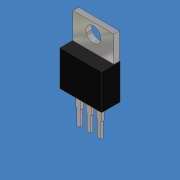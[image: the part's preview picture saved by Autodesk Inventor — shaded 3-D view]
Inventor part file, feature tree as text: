
AUTODESK INVENTOR PART (.ipt)
format: ipt  version: 2014 SP1 (Build 180222100, 222)  size: 157,184 bytes
history: native  units: mm (DEFAULTED — no unit token found)
features: sketch x5, extrude x4, hole x1, pattern_linear x1
ambient origin geometry x8: Origin, YZ Plane, XZ Plane, XY Plane, X Axis, Y Axis, Z Axis, Center Point
bodies: Solid1 (feature_tree)
feature tree (11):
  extrude  "Extrusion1"  Depth=8.636mm
  extrude  "Extrusion2"  Depth=6.35mm TaperAngle=0.0deg
  hole  "Hole1"  [1 undecoded]
  extrude  "Extrusion3"  Depth=0.5842mm
  extrude  "Extrusion4"  Depth=1.27mm
  pattern_linear  "Rectangular Pattern1"  Spacing1=1.905mm  [1 undecoded]
  sketch  "Sketch1"  dims[d0=10.16mm d1=8.636mm]
  sketch  "Sketch2"  dims[d2=4.4704mm d3=0.0mm d5=6.35mm d6=0.0mm]
  sketch  "Sketch3"  dims[d7=1.397mm d8=9.9822mm]
  sketch  "Sketch4"  dims[d9=2.54mm]
  sketch  "Sketch5"  dims[d10=3.683mm d11=12.7mm d12=9.525mm d13=6.35mm d14=14.3117mm d15=19.05mm d16=20.594885mm d17=0.5842mm d18=1.27mm d19=1.905mm d20=3.81mm d21=0.0mm d22=0.8128mm d23=3.81mm d24=0.0mm d25=30.0mm d27=2.54mm]
note: 2 required parameter values undecoded (feature->parameter linkage not recoverable at this tier; creation-order binding heuristic only, values carry confidence <= 0.55)
